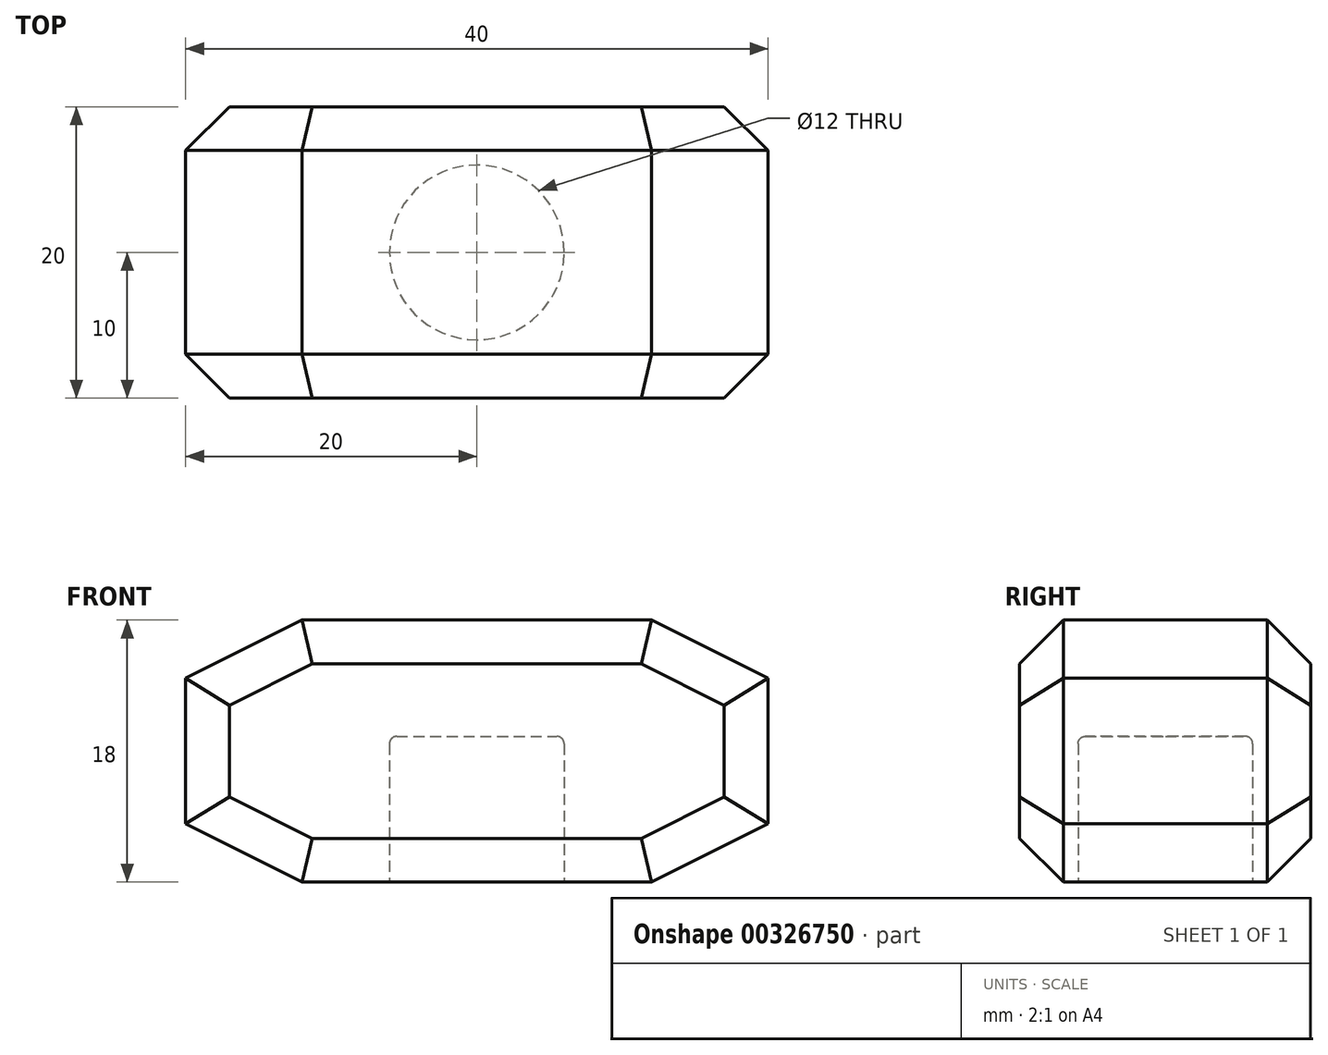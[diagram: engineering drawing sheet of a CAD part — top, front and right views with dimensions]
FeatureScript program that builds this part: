
annotation { "Feature Type Name" : "Feature", "Feature Type Description" : "" }
export const myFeature = defineFeature(function(context is Context, id is Id, definition is map)
    precondition{}
    {
        {
            var Q0;
            Q0=qCreatedBy(makeId("Front.planeOp"),FACE);
            var sketch = newSketch(context, id + "F0", { "sketchPlane" : qUnion([Q0])});
            skLineSegment(sketch, "E0.bottom", {"start": v(8, 0) * mm, "end": v(32, 0) * mm});
            skLineSegment(sketch, "E0.top", {"start": v(8, 18) * mm, "end": v(32, 18) * mm});
            skLineSegment(sketch, "E0.left", {"start": v(0, 4) * mm, "end": v(0, 14) * mm});
            skLineSegment(sketch, "E0.right", {"start": v(40, 4) * mm, "end": v(40, 14) * mm});
            skLineSegment(sketch, "E1", {"start": v(8, 18) * mm, "end": v(0, 14) * mm});
            skLineSegment(sketch, "E2", {"start": v(0, 4) * mm, "end": v(8, 0) * mm});
            skLineSegment(sketch, "E3", {"start": v(32, 0) * mm, "end": v(40, 4) * mm});
            skLineSegment(sketch, "E4", {"start": v(40, 14) * mm, "end": v(32, 18) * mm});
            skPoint(sketch, "E5.orphan", {"position": v(0, 18) * mm});
            skPoint(sketch, "E6.orphan", {"position": v(0, 0) * mm});
            skPoint(sketch, "E7.orphan", {"position": v(40, 18) * mm});
            skSolve(sketch);
        }
        {
            var Q0;
            Q0 = qSketchRegion(id + "F0", true);
            extrude(context, id + "F1", {"entities" : qUnion([Q0]), "depth" : 20 * mm});
        }
        {
            var Q0;
            Q0=makeQuery(id+"F1.opExtrude","CAP_FACE",FACE,{"disambiguationData":[OSD([sQuery(id+"F0.wireOp",EDGE,"E0.bottom"),sQuery(id+"F0.wireOp",EDGE,"E0.top"),sQuery(id+"F0.wireOp",EDGE,"E0.left"),sQuery(id+"F0.wireOp",EDGE,"E0.right"),sQuery(id+"F0.wireOp",EDGE,"E1"),sQuery(id+"F0.wireOp",EDGE,"E2"),sQuery(id+"F0.wireOp",EDGE,"E3"),sQuery(id+"F0.wireOp",EDGE,"E4")])],"isStart":false});
            var Q1;
            Q1=makeQuery(id+"F1.opExtrude","CAP_FACE",FACE,{"disambiguationData":[OSD([sQuery(id+"F0.wireOp",EDGE,"E0.bottom"),sQuery(id+"F0.wireOp",EDGE,"E0.top"),sQuery(id+"F0.wireOp",EDGE,"E0.left"),sQuery(id+"F0.wireOp",EDGE,"E0.right"),sQuery(id+"F0.wireOp",EDGE,"E1"),sQuery(id+"F0.wireOp",EDGE,"E2"),sQuery(id+"F0.wireOp",EDGE,"E3"),sQuery(id+"F0.wireOp",EDGE,"E4")])],"isStart":true});
            chamfer(context, id + "F2", {"entities" : qUnion([Q0, Q1]), "width" : 3 * mm, "tangentPropagation" : true});
        }
        {
            var Q0;
            Q0=makeQuery(id+"F1.opExtrude","SWEPT_FACE",FACE,{"disambiguationData":[OSD([sQuery(id+"F0.wireOp",EDGE,"E0.bottom")])]});
            var sketch = newSketch(context, id + "F3", { "sketchPlane" : qUnion([Q0])});
            skCircle(sketch, "E8", {"center": v(20, 10) * mm, "radius": 6 * mm});
            skPoint(sketch, "E8.centerSnap0", {"position": v(20, 17) * mm});
            skPoint(sketch, "E8.centerSnap1", {"position": v(8, 10) * mm});
            skSolve(sketch);
        }
        {
            var Q0;
            Q0=makeQuery(id+"F3.imprint","IMPRINT",FACE,{"disambiguationData":[TD([[makeQuery(id+"F3.imprint","IMPRINT",EDGE,{"derivedFrom":sQuery(id+"F3.wireOp",EDGE,"E8")}),1.0]])]});
            extrude(context, id + "F4", {"entities" : qUnion([Q0]), "operationType" : NewBodyOperationType.REMOVE, "oppositeDirection" : true, "depth" : 10 * mm});
        }
        {
            var Q0;
            Q0=makeQuery(id+"F4.boolean.opBoolean","COPY",EDGE,{"derivedFrom":makeQuery(id+"F4.opExtrude","CAP_EDGE",EDGE,{"disambiguationData":[OSD([sQuery(id+"F3.wireOp",EDGE,"E8")])],"isStart":false})});
            fillet(context, id + "F5", {"entities" : qUnion([Q0]), "radius" : .5 * mm, "tangentPropagation" : true, "allowEdgeOverflow" : false});
        }
    });
